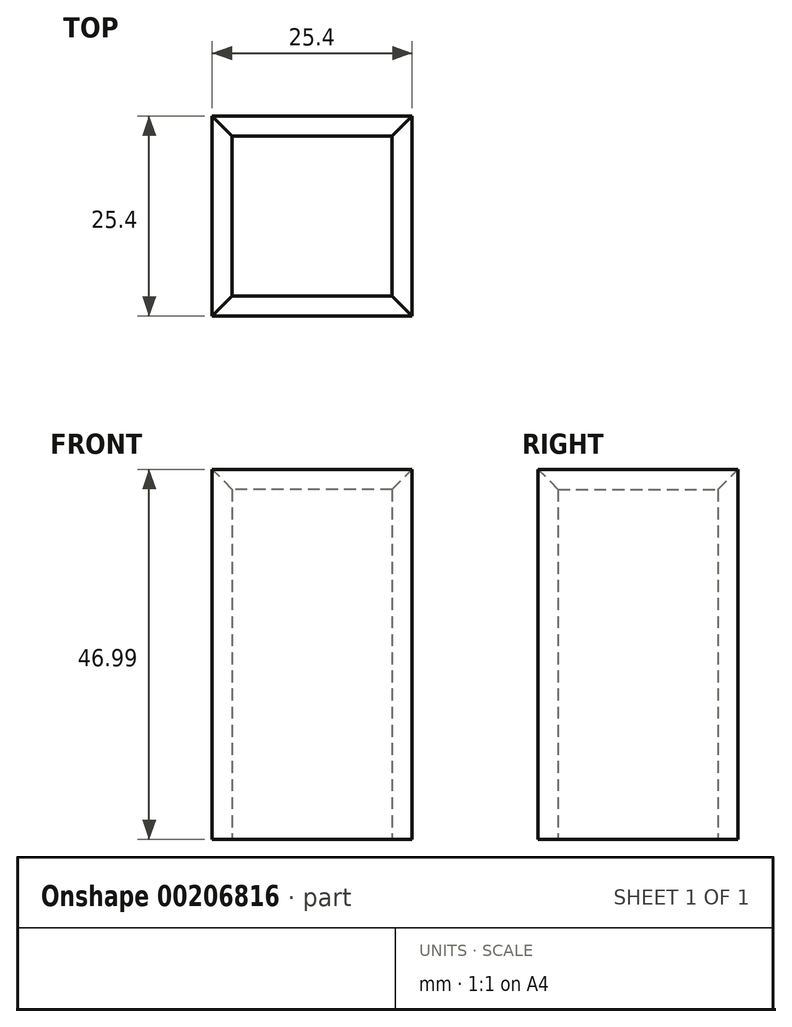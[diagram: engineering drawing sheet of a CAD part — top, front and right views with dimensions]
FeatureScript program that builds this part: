
annotation { "Feature Type Name" : "Feature", "Feature Type Description" : "" }
export const myFeature = defineFeature(function(context is Context, id is Id, definition is map)
    precondition{}
    {
        {
            var Q0;
            Q0=qCreatedBy(makeId("Top.planeOp"),FACE);
            var sketch = newSketch(context, id + "F0", { "sketchPlane" : qUnion([Q0])});
            skLineSegment(sketch, "E0.bottom", {"start": v(12.7, -12.7) * mm, "end": v(-12.7, -12.7) * mm});
            skLineSegment(sketch, "E0.top", {"start": v(12.7, 12.7) * mm, "end": v(-12.7, 12.7) * mm});
            skLineSegment(sketch, "E0.left", {"start": v(12.7, -12.7) * mm, "end": v(12.7, 12.7) * mm});
            skLineSegment(sketch, "E0.right", {"start": v(-12.7, -12.7) * mm, "end": v(-12.7, 12.7) * mm});
            skPoint(sketch, "E0.middle", {"position": v(0, 0) * mm});
            skLineSegment(sketch, "E1.0", {"start": v(10.16, 10.16) * mm, "end": v(-10.16, 10.16) * mm});
            skLineSegment(sketch, "E1.1", {"start": v(10.16, -10.16) * mm, "end": v(10.16, 10.16) * mm});
            skLineSegment(sketch, "E1.2", {"start": v(10.16, -10.16) * mm, "end": v(-10.16, -10.16) * mm});
            skLineSegment(sketch, "E1.3", {"start": v(-10.16, -10.16) * mm, "end": v(-10.16, 10.16) * mm});
            skSolve(sketch);
        }
        {
            var Q0;
            Q0=makeQuery(id+"F0.imprint","IMPRINT",FACE,{"disambiguationData":[TD([[makeQuery(id+"F0.imprint","IMPRINT",EDGE,{"derivedFrom":sQuery(id+"F0.wireOp",EDGE,"E0.bottom")}),-1.0]])]});
            extrude(context, id + "F1", {"entities" : qUnion([Q0]), "depth" : 50.8 * mm});
        }
        {
            var Q0;
            Q0=makeQuery(id+"F1.opExtrude","CAP_EDGE",EDGE,{"disambiguationData":[OSD([sQuery(id+"F0.wireOp",EDGE,"E1.3")])],"isStart":false});
            var Q1;
            Q1=makeQuery(id+"F1.opExtrude","CAP_EDGE",EDGE,{"disambiguationData":[OSD([sQuery(id+"F0.wireOp",EDGE,"E1.1")])],"isStart":false});
            var Q2;
            Q2=makeQuery(id+"F1.opExtrude","CAP_EDGE",EDGE,{"disambiguationData":[OSD([sQuery(id+"F0.wireOp",EDGE,"E1.2")])],"isStart":false});
            var Q3;
            Q3=makeQuery(id+"F1.opExtrude","CAP_EDGE",EDGE,{"disambiguationData":[OSD([sQuery(id+"F0.wireOp",EDGE,"E1.0")])],"isStart":false});
            chamfer(context, id + "F2", {"entities" : qUnion([Q0, Q1, Q2, Q3]), "chamferType" : ChamferType.OFFSET_ANGLE, "width" : 6.35 * mm, "oppositeDirection" : false, "angle" : 45 * degree, "tangentPropagation" : true});
        }
    });
